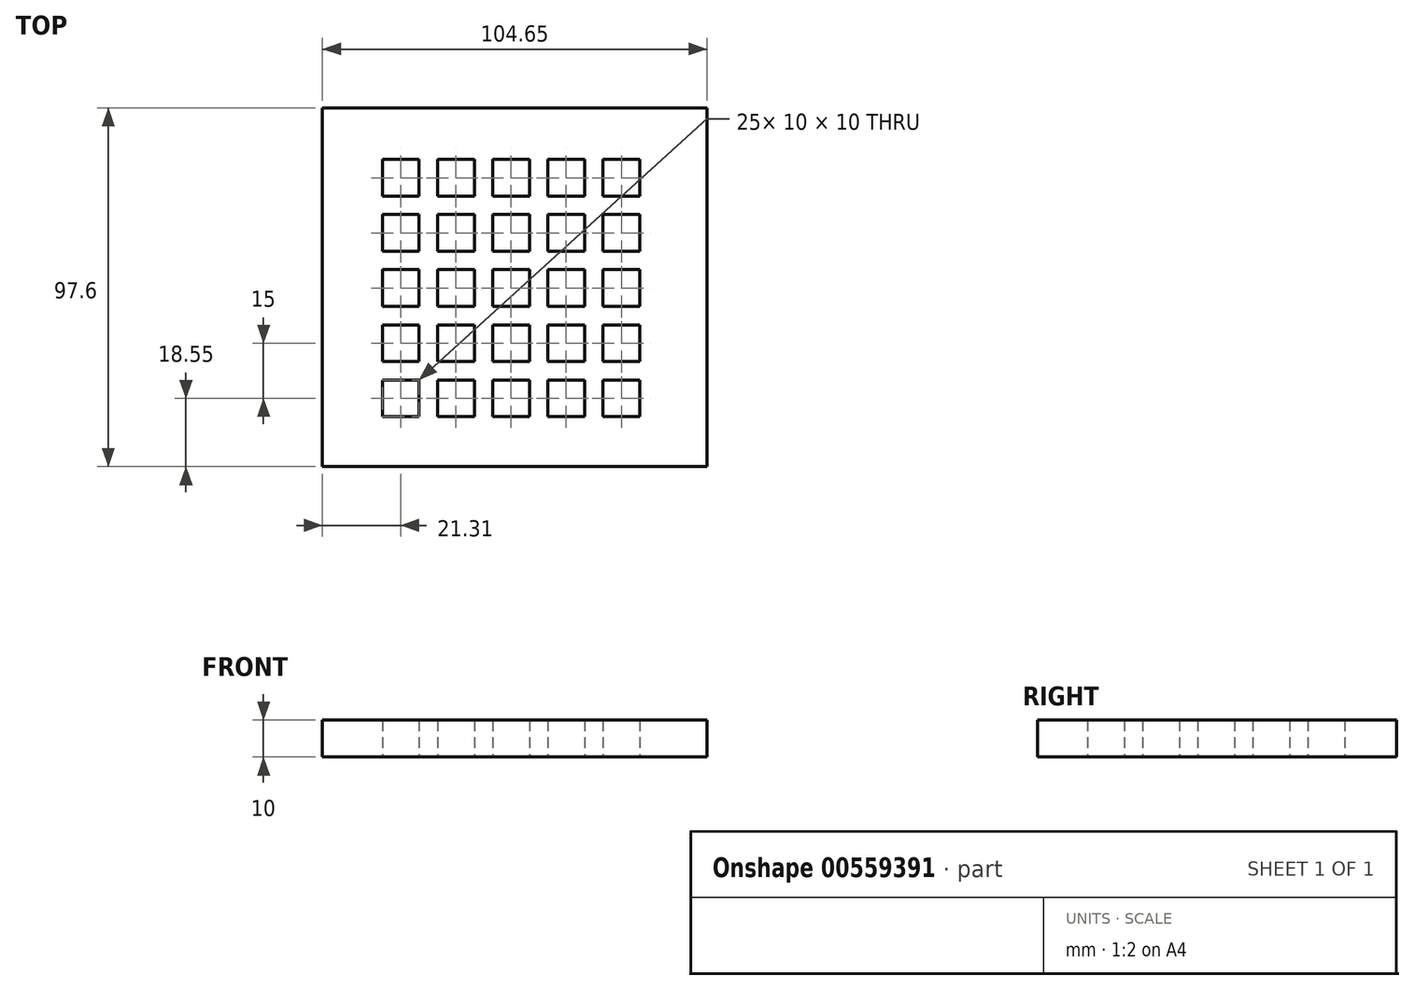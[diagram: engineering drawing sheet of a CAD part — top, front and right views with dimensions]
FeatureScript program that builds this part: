
annotation { "Feature Type Name" : "Feature", "Feature Type Description" : "" }
export const myFeature = defineFeature(function(context is Context, id is Id, definition is map)
    precondition{}
    {
        {
            var Q0;
            Q0=qCreatedBy(makeId("Top.planeOp"),FACE);
            var sketch = newSketch(context, id + "F0", { "sketchPlane" : qUnion([Q0])});
            skLineSegment(sketch, "E0.bottom", {"start": v(0, 0) * mm, "end": v(-10, 0) * mm});
            skLineSegment(sketch, "E0.top", {"start": v(0, 10) * mm, "end": v(-10, 10) * mm});
            skLineSegment(sketch, "E0.left", {"start": v(0, 0) * mm, "end": v(0, 10) * mm});
            skLineSegment(sketch, "E0.right", {"start": v(-10, 0) * mm, "end": v(-10, 10) * mm});
            skLineSegment(sketch, "E1.0.1.0", {"start": v(-10, 15) * mm, "end": v(-10, 25) * mm});
            skLineSegment(sketch, "E1.0.1.1", {"start": v(0, 15) * mm, "end": v(0, 25) * mm});
            skLineSegment(sketch, "E1.0.1.2", {"start": v(0, 25) * mm, "end": v(-10, 25) * mm});
            skLineSegment(sketch, "E1.0.1.3", {"start": v(0, 15) * mm, "end": v(-10, 15) * mm});
            skLineSegment(sketch, "E1.0.2.0", {"start": v(-10, 30) * mm, "end": v(-10, 40) * mm});
            skLineSegment(sketch, "E1.0.2.1", {"start": v(0, 30) * mm, "end": v(0, 40) * mm});
            skLineSegment(sketch, "E1.0.2.2", {"start": v(0, 40) * mm, "end": v(-10, 40) * mm});
            skLineSegment(sketch, "E1.0.2.3", {"start": v(0, 30) * mm, "end": v(-10, 30) * mm});
            skLineSegment(sketch, "E1.0.3.0", {"start": v(-10, 45) * mm, "end": v(-10, 55) * mm});
            skLineSegment(sketch, "E1.0.3.1", {"start": v(0, 45) * mm, "end": v(0, 55) * mm});
            skLineSegment(sketch, "E1.0.3.2", {"start": v(0, 55) * mm, "end": v(-10, 55) * mm});
            skLineSegment(sketch, "E1.0.3.3", {"start": v(0, 45) * mm, "end": v(-10, 45) * mm});
            skLineSegment(sketch, "E1.0.4.0", {"start": v(-10, 60) * mm, "end": v(-10, 70) * mm});
            skLineSegment(sketch, "E1.0.4.1", {"start": v(0, 60) * mm, "end": v(0, 70) * mm});
            skLineSegment(sketch, "E1.0.4.2", {"start": v(0, 70) * mm, "end": v(-10, 70) * mm});
            skLineSegment(sketch, "E1.0.4.3", {"start": v(0, 60) * mm, "end": v(-10, 60) * mm});
            skLineSegment(sketch, "E1.1.0.0", {"start": v(5, 0) * mm, "end": v(5, 10) * mm});
            skLineSegment(sketch, "E1.1.0.1", {"start": v(15, 0) * mm, "end": v(15, 10) * mm});
            skLineSegment(sketch, "E1.1.0.2", {"start": v(15, 10) * mm, "end": v(5, 10) * mm});
            skLineSegment(sketch, "E1.1.0.3", {"start": v(15, 0) * mm, "end": v(5, 0) * mm});
            skLineSegment(sketch, "E1.1.1.0", {"start": v(5, 15) * mm, "end": v(5, 25) * mm});
            skLineSegment(sketch, "E1.1.1.1", {"start": v(15, 15) * mm, "end": v(15, 25) * mm});
            skLineSegment(sketch, "E1.1.1.2", {"start": v(15, 25) * mm, "end": v(5, 25) * mm});
            skLineSegment(sketch, "E1.1.1.3", {"start": v(15, 15) * mm, "end": v(5, 15) * mm});
            skLineSegment(sketch, "E1.1.2.0", {"start": v(5, 30) * mm, "end": v(5, 40) * mm});
            skLineSegment(sketch, "E1.1.2.1", {"start": v(15, 30) * mm, "end": v(15, 40) * mm});
            skLineSegment(sketch, "E1.1.2.2", {"start": v(15, 40) * mm, "end": v(5, 40) * mm});
            skLineSegment(sketch, "E1.1.2.3", {"start": v(15, 30) * mm, "end": v(5, 30) * mm});
            skLineSegment(sketch, "E1.1.3.0", {"start": v(5, 45) * mm, "end": v(5, 55) * mm});
            skLineSegment(sketch, "E1.1.3.1", {"start": v(15, 45) * mm, "end": v(15, 55) * mm});
            skLineSegment(sketch, "E1.1.3.2", {"start": v(15, 55) * mm, "end": v(5, 55) * mm});
            skLineSegment(sketch, "E1.1.3.3", {"start": v(15, 45) * mm, "end": v(5, 45) * mm});
            skLineSegment(sketch, "E1.1.4.0", {"start": v(5, 60) * mm, "end": v(5, 70) * mm});
            skLineSegment(sketch, "E1.1.4.1", {"start": v(15, 60) * mm, "end": v(15, 70) * mm});
            skLineSegment(sketch, "E1.1.4.2", {"start": v(15, 70) * mm, "end": v(5, 70) * mm});
            skLineSegment(sketch, "E1.1.4.3", {"start": v(15, 60) * mm, "end": v(5, 60) * mm});
            skLineSegment(sketch, "E1.2.0.0", {"start": v(20, 0) * mm, "end": v(20, 10) * mm});
            skLineSegment(sketch, "E1.2.0.1", {"start": v(30, 0) * mm, "end": v(30, 10) * mm});
            skLineSegment(sketch, "E1.2.0.2", {"start": v(30, 10) * mm, "end": v(20, 10) * mm});
            skLineSegment(sketch, "E1.2.0.3", {"start": v(30, 0) * mm, "end": v(20, 0) * mm});
            skLineSegment(sketch, "E1.2.1.0", {"start": v(20, 15) * mm, "end": v(20, 25) * mm});
            skLineSegment(sketch, "E1.2.1.1", {"start": v(30, 15) * mm, "end": v(30, 25) * mm});
            skLineSegment(sketch, "E1.2.1.2", {"start": v(30, 25) * mm, "end": v(20, 25) * mm});
            skLineSegment(sketch, "E1.2.1.3", {"start": v(30, 15) * mm, "end": v(20, 15) * mm});
            skLineSegment(sketch, "E1.2.2.0", {"start": v(20, 30) * mm, "end": v(20, 40) * mm});
            skLineSegment(sketch, "E1.2.2.1", {"start": v(30, 30) * mm, "end": v(30, 40) * mm});
            skLineSegment(sketch, "E1.2.2.2", {"start": v(30, 40) * mm, "end": v(20, 40) * mm});
            skLineSegment(sketch, "E1.2.2.3", {"start": v(30, 30) * mm, "end": v(20, 30) * mm});
            skLineSegment(sketch, "E1.2.3.0", {"start": v(20, 45) * mm, "end": v(20, 55) * mm});
            skLineSegment(sketch, "E1.2.3.1", {"start": v(30, 45) * mm, "end": v(30, 55) * mm});
            skLineSegment(sketch, "E1.2.3.2", {"start": v(30, 55) * mm, "end": v(20, 55) * mm});
            skLineSegment(sketch, "E1.2.3.3", {"start": v(30, 45) * mm, "end": v(20, 45) * mm});
            skLineSegment(sketch, "E1.2.4.0", {"start": v(20, 60) * mm, "end": v(20, 70) * mm});
            skLineSegment(sketch, "E1.2.4.1", {"start": v(30, 60) * mm, "end": v(30, 70) * mm});
            skLineSegment(sketch, "E1.2.4.2", {"start": v(30, 70) * mm, "end": v(20, 70) * mm});
            skLineSegment(sketch, "E1.2.4.3", {"start": v(30, 60) * mm, "end": v(20, 60) * mm});
            skLineSegment(sketch, "E1.3.0.0", {"start": v(35, 0) * mm, "end": v(35, 10) * mm});
            skLineSegment(sketch, "E1.3.0.1", {"start": v(45, 0) * mm, "end": v(45, 10) * mm});
            skLineSegment(sketch, "E1.3.0.2", {"start": v(45, 10) * mm, "end": v(35, 10) * mm});
            skLineSegment(sketch, "E1.3.0.3", {"start": v(45, 0) * mm, "end": v(35, 0) * mm});
            skLineSegment(sketch, "E1.3.1.0", {"start": v(35, 15) * mm, "end": v(35, 25) * mm});
            skLineSegment(sketch, "E1.3.1.1", {"start": v(45, 15) * mm, "end": v(45, 25) * mm});
            skLineSegment(sketch, "E1.3.1.2", {"start": v(45, 25) * mm, "end": v(35, 25) * mm});
            skLineSegment(sketch, "E1.3.1.3", {"start": v(45, 15) * mm, "end": v(35, 15) * mm});
            skLineSegment(sketch, "E1.3.2.0", {"start": v(35, 30) * mm, "end": v(35, 40) * mm});
            skLineSegment(sketch, "E1.3.2.1", {"start": v(45, 30) * mm, "end": v(45, 40) * mm});
            skLineSegment(sketch, "E1.3.2.2", {"start": v(45, 40) * mm, "end": v(35, 40) * mm});
            skLineSegment(sketch, "E1.3.2.3", {"start": v(45, 30) * mm, "end": v(35, 30) * mm});
            skLineSegment(sketch, "E1.3.3.0", {"start": v(35, 45) * mm, "end": v(35, 55) * mm});
            skLineSegment(sketch, "E1.3.3.1", {"start": v(45, 45) * mm, "end": v(45, 55) * mm});
            skLineSegment(sketch, "E1.3.3.2", {"start": v(45, 55) * mm, "end": v(35, 55) * mm});
            skLineSegment(sketch, "E1.3.3.3", {"start": v(45, 45) * mm, "end": v(35, 45) * mm});
            skLineSegment(sketch, "E1.3.4.0", {"start": v(35, 60) * mm, "end": v(35, 70) * mm});
            skLineSegment(sketch, "E1.3.4.1", {"start": v(45, 60) * mm, "end": v(45, 70) * mm});
            skLineSegment(sketch, "E1.3.4.2", {"start": v(45, 70) * mm, "end": v(35, 70) * mm});
            skLineSegment(sketch, "E1.3.4.3", {"start": v(45, 60) * mm, "end": v(35, 60) * mm});
            skLineSegment(sketch, "E1.4.0.0", {"start": v(50, 0) * mm, "end": v(50, 10) * mm});
            skLineSegment(sketch, "E1.4.0.1", {"start": v(60, 0) * mm, "end": v(60, 10) * mm});
            skLineSegment(sketch, "E1.4.0.2", {"start": v(60, 10) * mm, "end": v(50, 10) * mm});
            skLineSegment(sketch, "E1.4.0.3", {"start": v(60, 0) * mm, "end": v(50, 0) * mm});
            skLineSegment(sketch, "E1.4.1.0", {"start": v(50, 15) * mm, "end": v(50, 25) * mm});
            skLineSegment(sketch, "E1.4.1.1", {"start": v(60, 15) * mm, "end": v(60, 25) * mm});
            skLineSegment(sketch, "E1.4.1.2", {"start": v(60, 25) * mm, "end": v(50, 25) * mm});
            skLineSegment(sketch, "E1.4.1.3", {"start": v(60, 15) * mm, "end": v(50, 15) * mm});
            skLineSegment(sketch, "E1.4.2.0", {"start": v(50, 30) * mm, "end": v(50, 40) * mm});
            skLineSegment(sketch, "E1.4.2.1", {"start": v(60, 30) * mm, "end": v(60, 40) * mm});
            skLineSegment(sketch, "E1.4.2.2", {"start": v(60, 40) * mm, "end": v(50, 40) * mm});
            skLineSegment(sketch, "E1.4.2.3", {"start": v(60, 30) * mm, "end": v(50, 30) * mm});
            skLineSegment(sketch, "E1.4.3.0", {"start": v(50, 45) * mm, "end": v(50, 55) * mm});
            skLineSegment(sketch, "E1.4.3.1", {"start": v(60, 45) * mm, "end": v(60, 55) * mm});
            skLineSegment(sketch, "E1.4.3.2", {"start": v(60, 55) * mm, "end": v(50, 55) * mm});
            skLineSegment(sketch, "E1.4.3.3", {"start": v(60, 45) * mm, "end": v(50, 45) * mm});
            skLineSegment(sketch, "E1.4.4.0", {"start": v(50, 60) * mm, "end": v(50, 70) * mm});
            skLineSegment(sketch, "E1.4.4.1", {"start": v(60, 60) * mm, "end": v(60, 70) * mm});
            skLineSegment(sketch, "E1.4.4.2", {"start": v(60, 70) * mm, "end": v(50, 70) * mm});
            skLineSegment(sketch, "E1.4.4.3", {"start": v(60, 60) * mm, "end": v(50, 60) * mm});
            skLineSegment(sketch, "E1.direction1", {"start": v(-10, 0) * mm, "end": v(5, 0) * mm, "construction": true});
            skLineSegment(sketch, "E1.direction2", {"start": v(-10, 0) * mm, "end": v(-10, 15) * mm, "construction": true});
            skSolve(sketch);
        }
        {
            var Q0;
            Q0=qCreatedBy(makeId("Top.planeOp"),FACE);
            var sketch = newSketch(context, id + "F1", { "sketchPlane" : qUnion([Q0])});
            skLineSegment(sketch, "E2.bottom", {"start": v(-26.3, -13.55) * mm, "end": v(78.34, -13.55) * mm});
            skLineSegment(sketch, "E2.top", {"start": v(-26.3, 84.05) * mm, "end": v(78.34, 84.05) * mm});
            skLineSegment(sketch, "E2.left", {"start": v(-26.3, -13.55) * mm, "end": v(-26.3, 84.05) * mm});
            skLineSegment(sketch, "E2.right", {"start": v(78.34, -13.55) * mm, "end": v(78.34, 84.05) * mm});
            skSolve(sketch);
        }
        {
            var Q0;
            Q0 = qSketchRegion(id + "F1", true);
            extrude(context, id + "F2", {"entities" : qUnion([Q0]), "depth" : 10 * mm, "offsetDistance" : 25 * mm});
        }
        {
            var Q0;
            Q0 = qSketchRegion(id + "F0", true);
            extrude(context, id + "F3", {"entities" : qUnion([Q0]), "operationType" : NewBodyOperationType.REMOVE, "depth" : 25 * mm, "offsetDistance" : 25 * mm});
        }
    });
